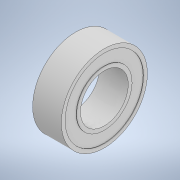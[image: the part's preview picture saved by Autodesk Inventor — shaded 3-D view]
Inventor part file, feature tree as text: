
AUTODESK INVENTOR PART (.ipt)
format: ipt  version: 2020 (Build 240168000, 168)  size: 129,536 bytes
history: native  units: mm
features: extrude x2, other x1, sketch x1
ambient origin geometry x8: Origin, YZ Plane, XZ Plane, XY Plane, X Axis, Y Axis, Z Axis, Center Point
bodies: Body1 (feature_tree)
feature tree (4):
  other  "Твердое тело1"
  sketch  "Эскиз1"
  extrude  "Выдавливание1"  Depth=5.0mm
  extrude  "Выдавливание2"  Depth=9.0mm
